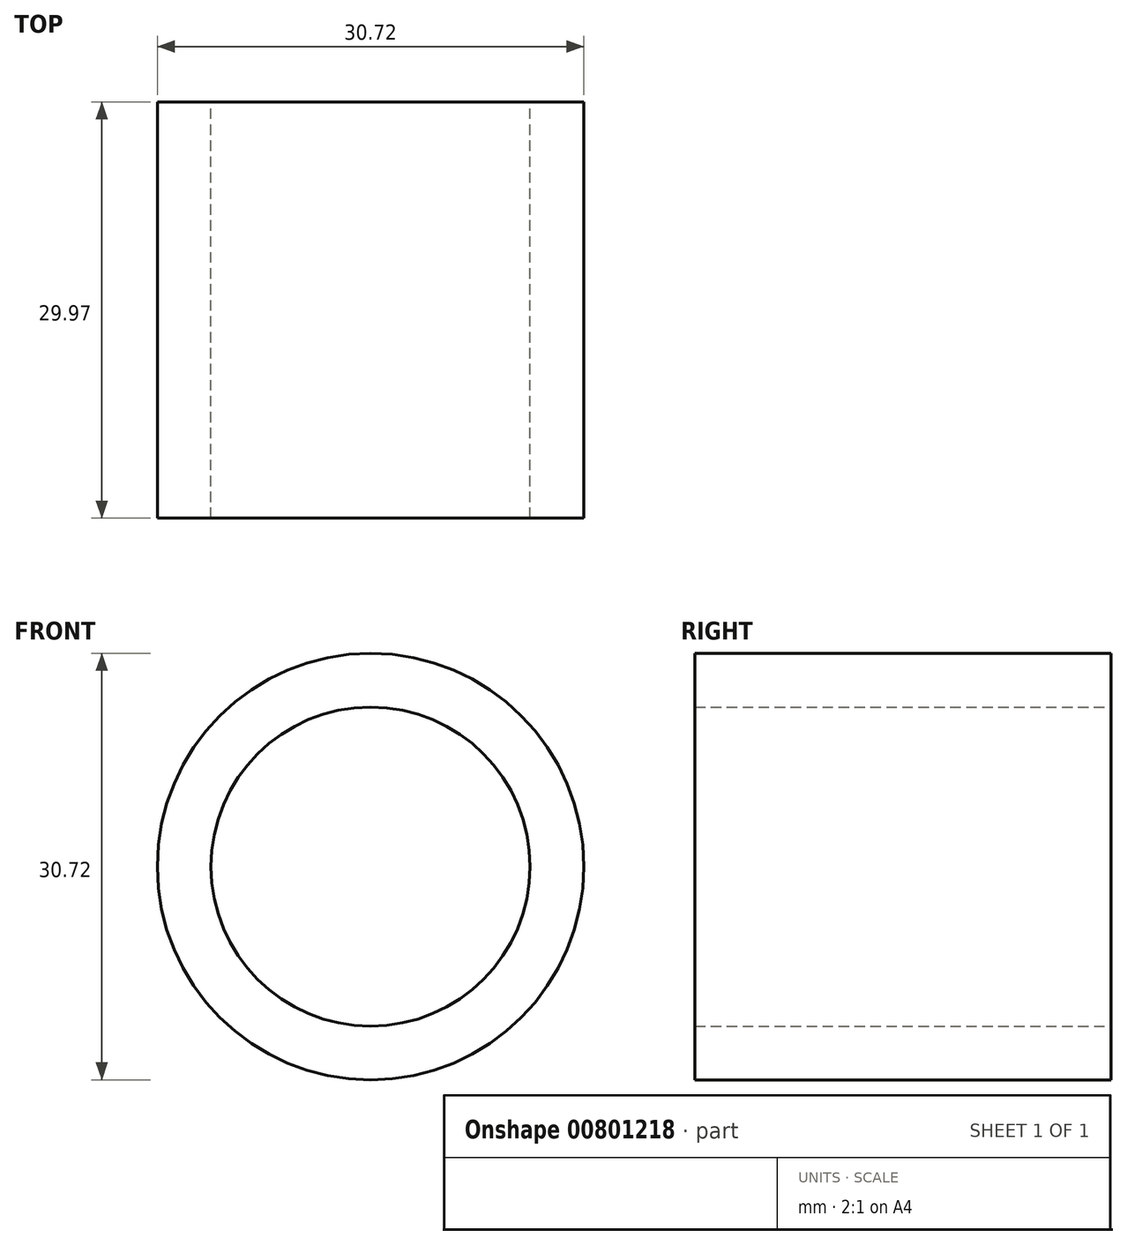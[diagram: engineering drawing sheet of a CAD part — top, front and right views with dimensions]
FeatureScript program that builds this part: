
annotation { "Feature Type Name" : "Feature", "Feature Type Description" : "" }
export const myFeature = defineFeature(function(context is Context, id is Id, definition is map)
    precondition{}
    {
        {
            var Q0;
            Q0=qCreatedBy(makeId("Front.planeOp"),FACE);
            var sketch = newSketch(context, id + "F0", { "sketchPlane" : qUnion([Q0])});
            skCircle(sketch, "E0", {"center": v(0, 0) * mm, "radius": 11.5 * mm});
            skCircle(sketch, "E1", {"center": v(0, 0) * mm, "radius": 15.36 * mm});
            skSolve(sketch);
        }
        {
            var Q0;
            Q0=makeQuery(id+"F0.imprint","IMPRINT",FACE,{"disambiguationData":[TD([[makeQuery(id+"F0.imprint","IMPRINT",EDGE,{"derivedFrom":sQuery(id+"F0.wireOp",EDGE,"E0")}),-1.0]])]});
            extrude(context, id + "F1", {"entities" : qUnion([Q0]), "depth" : 29.97 * mm, "offsetDistance" : 25.4 * mm});
        }
    });
